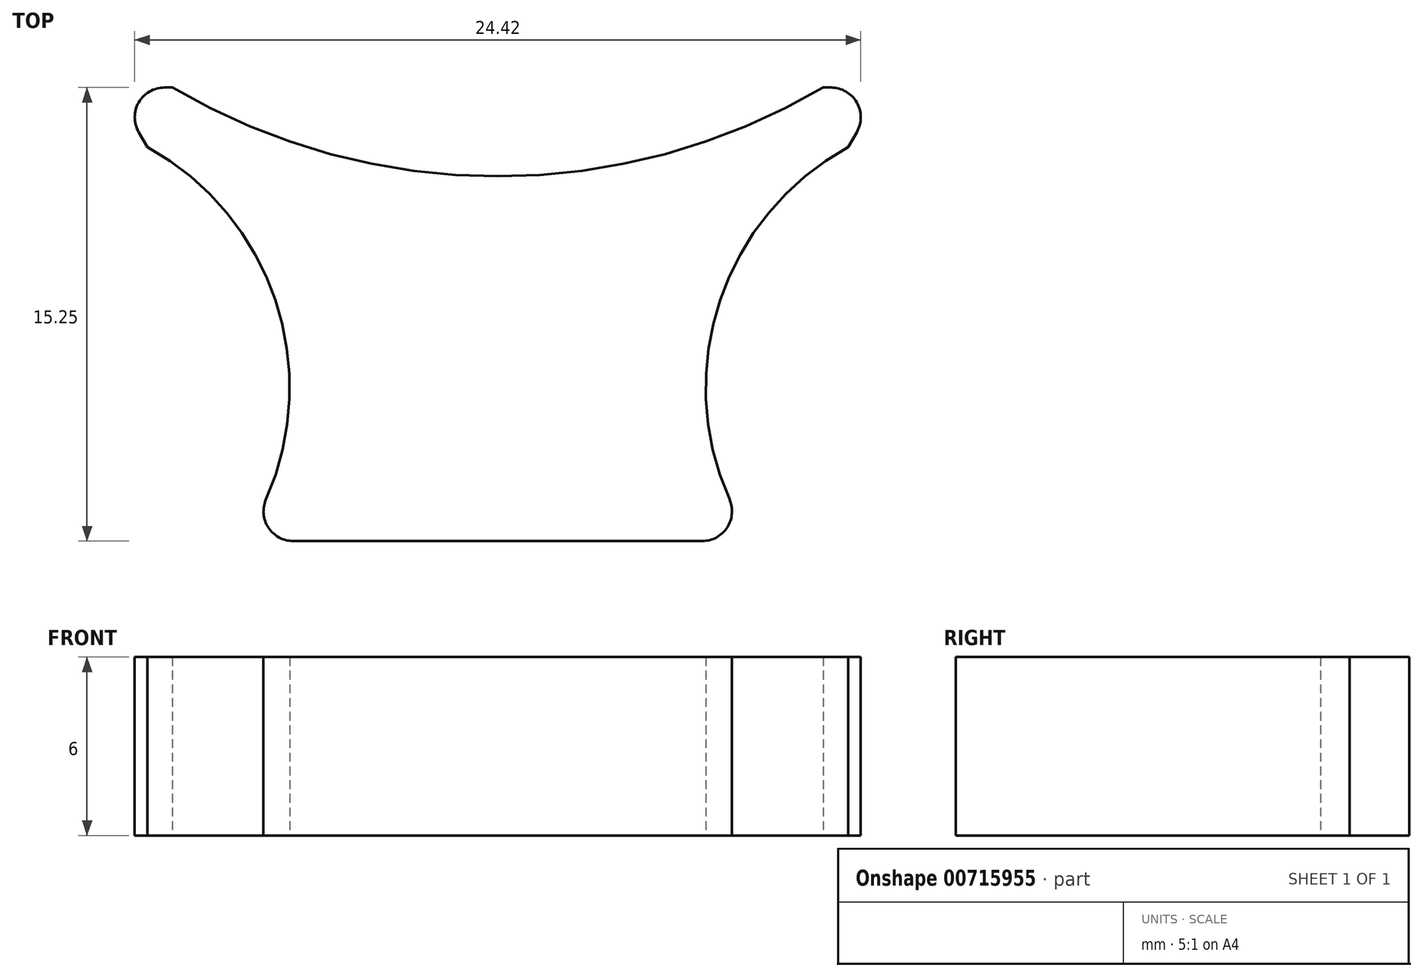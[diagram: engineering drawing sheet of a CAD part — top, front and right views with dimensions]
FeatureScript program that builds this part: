
annotation { "Feature Type Name" : "Feature", "Feature Type Description" : "" }
export const myFeature = defineFeature(function(context is Context, id is Id, definition is map)
    precondition{}
    {
        {
            var Q0;
            Q0=qCreatedBy(makeId("Top.planeOp"),FACE);
            var sketch = newSketch(context, id + "F0", { "sketchPlane" : qUnion([Q0])});
            skLineSegment(sketch, "E0", {"start": v(0, -31.5) * mm, "end": v(0, 39.08) * mm, "construction": true});
            skLineSegment(sketch, "E1", {"start": v(28.67, 0) * mm, "end": v(-28.37, 0) * mm, "construction": true});
            skLineSegment(sketch, "E2.MirrorCS", {"start": v(-11.79, 8.25) * mm, "end": v(-12.95, 10.25) * mm});
            skLineSegment(sketch, "E3.MirrorCS", {"start": v(-12.95, 10.25) * mm, "end": v(-10.95, 10.25) * mm});
            skLineSegment(sketch, "E4.MirrorCS", {"start": v(12.95, 10.25) * mm, "end": v(10.95, 10.25) * mm});
            skLineSegment(sketch, "E5.MirrorCS", {"start": v(11.79, 8.25) * mm, "end": v(12.95, 10.25) * mm});
            skLineSegment(sketch, "E6", {"start": v(-11.79, 8.25) * mm, "end": v(11.79, 8.25) * mm, "construction": true});
            skArc(sketch, "E7", {"start": v(-8.57, -5) * mm, "mid": v(-7.26, 2.33) * mm, "end": v(-11.79, 8.25) * mm});
            skArc(sketch, "E8.MirrorCS", {"start": v(8.57, -5) * mm, "mid": v(7.26, 2.33) * mm, "end": v(11.79, 8.25) * mm});
            skPoint(sketch, "E9.orphan", {"position": v(-7, 0) * mm});
            skPoint(sketch, "E10.orphan", {"position": v(7, 0) * mm});
            skLineSegment(sketch, "E11", {"start": v(-8.57, -5) * mm, "end": v(8.57, -5) * mm});
            skLineSegment(sketch, "E12", {"start": v(-10.95, 14.74) * mm, "end": v(-10.95, 3.9) * mm, "construction": true});
            skLineSegment(sketch, "E13.MirrorCS", {"start": v(10.95, 14.74) * mm, "end": v(10.95, 3.9) * mm, "construction": true});
            skArc(sketch, "E14", {"start": v(-10.95, 10.25) * mm, "mid": v(0, 7.27) * mm, "end": v(10.95, 10.25) * mm});
            skSolve(sketch);
        }
        {
            var Q0;
            Q0=makeQuery(id+"F0.imprint","IMPRINT",FACE,{"disambiguationData":[TD([[makeQuery(id+"F0.imprint","IMPRINT",EDGE,{"derivedFrom":sQuery(id+"F0.wireOp",EDGE,"PfhNlWNs-CzBl-nI37-9E01-fsLF7MDHO91B")}),1.0]])]});
            var Q1;
            Q1=makeQuery(id+"F0.imprint","IMPRINT",FACE,{"disambiguationData":[TD([[makeQuery(id+"F0.imprint","IMPRINT",EDGE,{"derivedFrom":sQuery(id+"F0.wireOp",EDGE,"E2.MirrorCS")}),-1.0]])]});
            extrude(context, id + "F1", {"entities" : qUnion([Q0, Q1]), "endBound" : BoundingType.SYMMETRIC, "depth" : 6 * mm, "offsetDistance" : 25 * mm});
        }
        {
            var Q0;
            Q0=makeQuery(id+"F1.opExtrude","SWEPT_EDGE",EDGE,{"disambiguationData":[OSD([sQuery(id+"F0.wireOp",EDGE,"E2.MirrorCS"),sQuery(id+"F0.wireOp",EDGE,"E3.MirrorCS")])]});
            var Q1;
            Q1=makeQuery(id+"F1.opExtrude","SWEPT_EDGE",EDGE,{"disambiguationData":[OSD([sQuery(id+"F0.wireOp",EDGE,"E4.MirrorCS"),sQuery(id+"F0.wireOp",EDGE,"E5.MirrorCS")])]});
            var Q2;
            Q2=makeQuery(id+"F1.opExtrude","SWEPT_EDGE",EDGE,{"disambiguationData":[OSD([sQuery(id+"F0.wireOp",EDGE,"E7"),sQuery(id+"F0.wireOp",EDGE,"E11")])]});
            var Q3;
            Q3=makeQuery(id+"F1.opExtrude","SWEPT_EDGE",EDGE,{"disambiguationData":[OSD([sQuery(id+"F0.wireOp",EDGE,"E8.MirrorCS"),sQuery(id+"F0.wireOp",EDGE,"E11")])]});
            fillet(context, id + "F2", {"entities" : qUnion([Q0, Q1, Q2, Q3]), "radius" : 1 * mm, "tangentPropagation" : true, "allowEdgeOverflow" : false});
        }
    });
